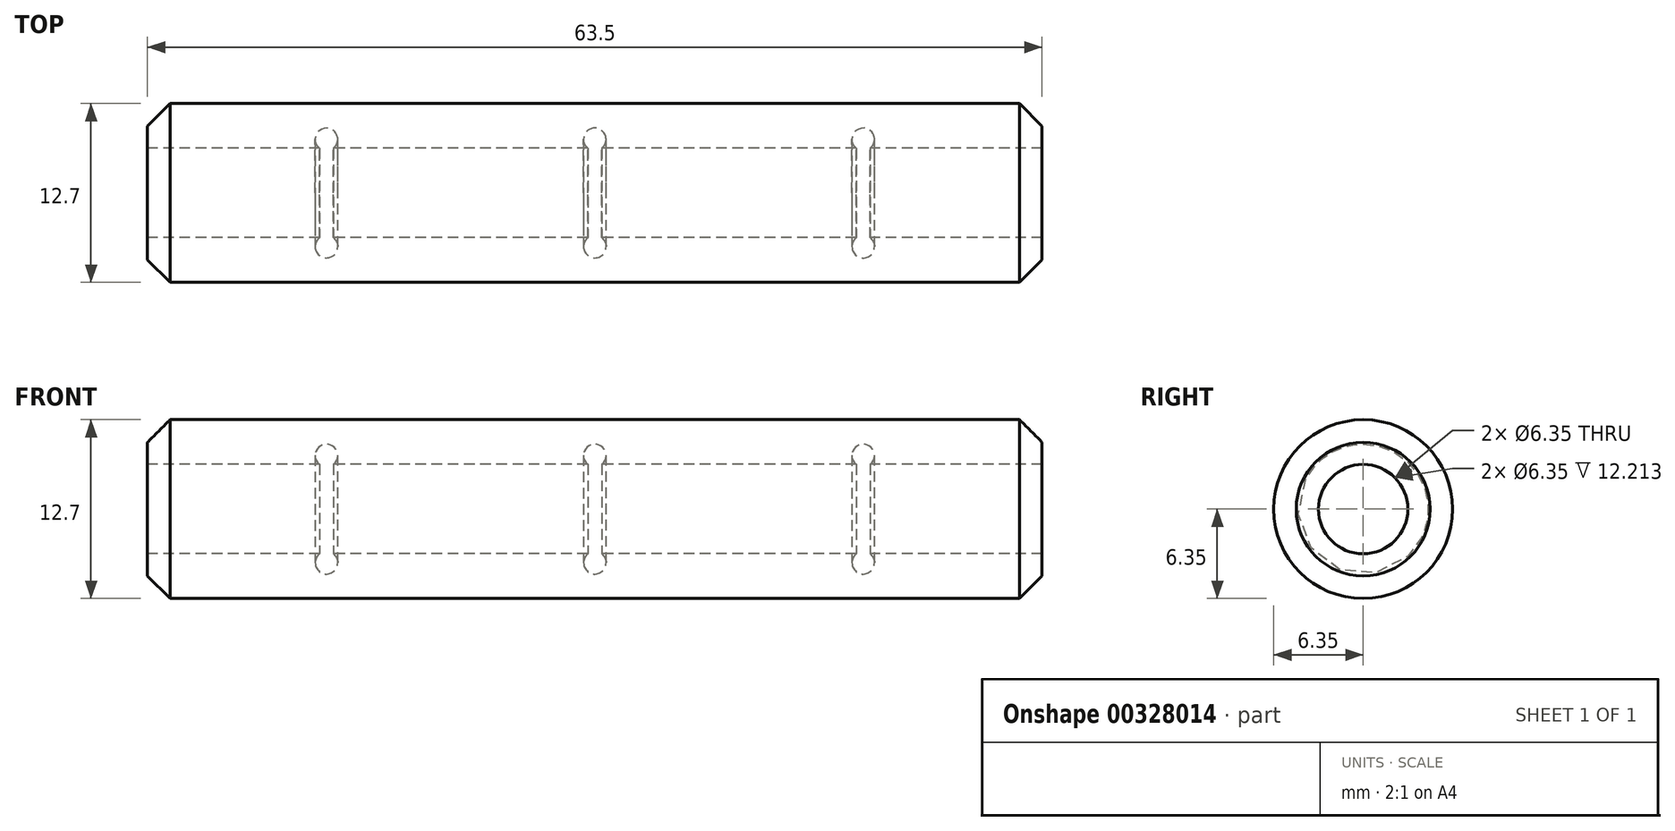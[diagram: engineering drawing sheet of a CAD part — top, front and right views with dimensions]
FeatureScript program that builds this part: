
annotation { "Feature Type Name" : "Feature", "Feature Type Description" : "" }
export const myFeature = defineFeature(function(context is Context, id is Id, definition is map)
    precondition{}
    {
        {
            var Q0;
            Q0=qCreatedBy(makeId("Front.planeOp"),FACE);
            var sketch = newSketch(context, id + "F0", { "sketchPlane" : qUnion([Q0])});
            skLineSegment(sketch, "E0.bottom", {"start": v(0, 3.18) * mm, "end": v(12.21, 3.18) * mm});
            skLineSegment(sketch, "E0.top", {"start": v(0, 6.35) * mm, "end": v(63.5, 6.35) * mm});
            skLineSegment(sketch, "E0.left", {"start": v(0, 3.18) * mm, "end": v(0, 6.35) * mm});
            skLineSegment(sketch, "E0.right", {"start": v(63.5, 3.18) * mm, "end": v(63.5, 6.35) * mm});
            skLineSegment(sketch, "E1", {"start": v(0, 0) * mm, "end": v(77.16, 0) * mm});
            skArc(sketch, "E2", {"start": v(32.24, 3.18) * mm, "mid": v(31.75, 4.61) * mm, "end": v(31.26, 3.18) * mm});
            skArc(sketch, "E3", {"start": v(51.29, 3.17) * mm, "mid": v(50.8, 4.61) * mm, "end": v(50.31, 3.17) * mm});
            skArc(sketch, "E4", {"start": v(13.19, 3.17) * mm, "mid": v(12.7, 4.61) * mm, "end": v(12.21, 3.18) * mm});
            skLineSegment(sketch, "E5.trimOffspring", {"start": v(13.19, 3.18) * mm, "end": v(31.26, 3.18) * mm});
            skLineSegment(sketch, "E6.trimOffspring", {"start": v(32.24, 3.18) * mm, "end": v(50.31, 3.18) * mm});
            skLineSegment(sketch, "E7.trimOffspring", {"start": v(51.29, 3.18) * mm, "end": v(63.5, 3.18) * mm});
            skSolve(sketch);
        }
        {
            var Q0;
            Q0=makeQuery(id+"F0.imprint","IMPRINT",FACE,{"disambiguationData":[TD([[makeQuery(id+"F0.imprint","IMPRINT",EDGE,{"derivedFrom":sQuery(id+"F0.wireOp",EDGE,"E0.bottom")}),1.0]])]});
            var Q1;
            Q1=sQuery(id+"F0.wireOp",EDGE,"E1");
            revolve(context, id + "F1", {"entities" : qUnion([Q0]), "axis" : qUnion([Q1]), "revolveType" : RevolveType.FULL});
        }
        {
            var Q0;
            Q0=makeQuery(id+"F1.opRevolve","SWEPT_EDGE",EDGE,{"disambiguationData":[OSD([sQuery(id+"F0.wireOp",EDGE,"E0.top"),sQuery(id+"F0.wireOp",EDGE,"E0.left")])]});
            var Q1;
            Q1=makeQuery(id+"F1.opRevolve","SWEPT_EDGE",EDGE,{"disambiguationData":[OSD([sQuery(id+"F0.wireOp",EDGE,"E0.top"),sQuery(id+"F0.wireOp",EDGE,"E0.right")])]});
            chamfer(context, id + "F2", {"entities" : qUnion([Q0, Q1]), "width" : 1.6 * mm, "tangentPropagation" : true});
        }
    });
